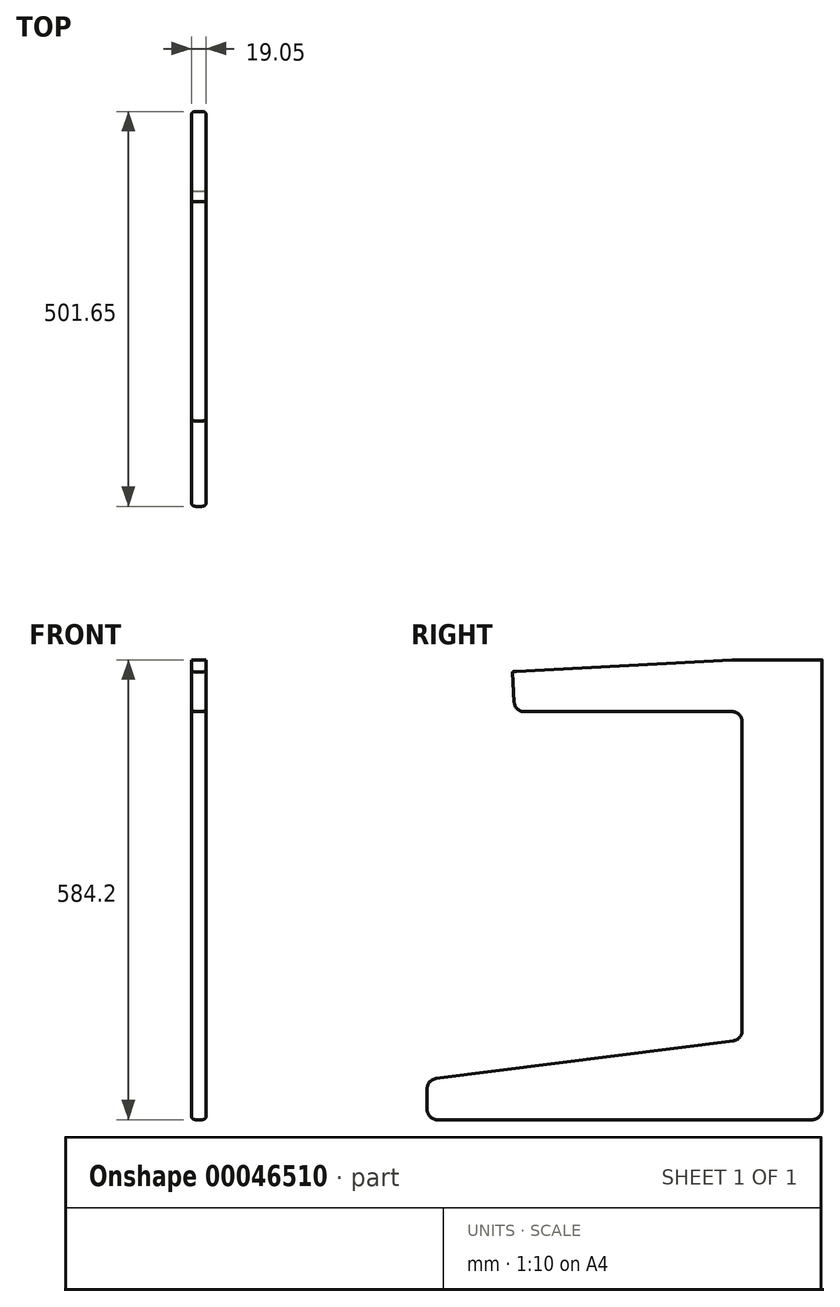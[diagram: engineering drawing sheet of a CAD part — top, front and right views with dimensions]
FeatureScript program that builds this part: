
annotation { "Feature Type Name" : "Feature", "Feature Type Description" : "" }
export const myFeature = defineFeature(function(context is Context, id is Id, definition is map)
    precondition{}
    {
        {
            var Q0;
            Q0=qCreatedBy(makeId("Right.planeOp"),FACE);
            var sketch = newSketch(context, id + "F0", { "sketchPlane" : qUnion([Q0])});
            skLineSegment(sketch, "E0", {"start": v(282.08, -321.8) * mm, "end": v(282.08, 249.7) * mm});
            skLineSegment(sketch, "E1", {"start": v(282.08, 249.7) * mm, "end": v(167.78, 249.7) * mm});
            skLineSegment(sketch, "E2", {"start": v(167.78, 249.7) * mm, "end": v(-111.2, 234.5) * mm});
            skLineSegment(sketch, "E3", {"start": v(-111.2, 234.5) * mm, "end": v(-109.1, 195.79) * mm});
            skLineSegment(sketch, "E4", {"start": v(-96.41, 183.78) * mm, "end": v(167.78, 183.78) * mm});
            skLineSegment(sketch, "E5", {"start": v(180.48, 171.08) * mm, "end": v(180.48, -221.72) * mm});
            skLineSegment(sketch, "E6", {"start": v(169.38, -234.32) * mm, "end": v(-208.47, -282.3) * mm});
            skLineSegment(sketch, "E7", {"start": v(-219.57, -294.9) * mm, "end": v(-219.57, -321.8) * mm});
            skLineSegment(sketch, "E8", {"start": v(-206.87, -334.5) * mm, "end": v(269.38, -334.5) * mm});
            skPoint(sketch, "E9.visualSharp", {"position": v(180.48, 183.78) * mm});
            skArc(sketch, "E9.filletArc", {"start": v(180.48, 171.08) * mm, "mid": v(176.76, 180.06) * mm, "end": v(167.78, 183.78) * mm});
            skPoint(sketch, "E10.visualSharp", {"position": v(-108.44, 183.78) * mm});
            skArc(sketch, "E10.filletArc", {"start": v(-109.1, 195.79) * mm, "mid": v(-105.15, 187.26) * mm, "end": v(-96.41, 183.78) * mm});
            skPoint(sketch, "E11.visualSharp", {"position": v(180.48, -232.9) * mm});
            skArc(sketch, "E11.filletArc", {"start": v(169.38, -234.32) * mm, "mid": v(177.31, -230.12) * mm, "end": v(180.48, -221.72) * mm});
            skPoint(sketch, "E12.visualSharp", {"position": v(-219.57, -283.7) * mm});
            skArc(sketch, "E12.filletArc", {"start": v(-208.47, -282.3) * mm, "mid": v(-216.4, -286.5) * mm, "end": v(-219.57, -294.9) * mm});
            skPoint(sketch, "E13.visualSharp", {"position": v(-219.57, -334.5) * mm});
            skArc(sketch, "E13.filletArc", {"start": v(-219.57, -321.8) * mm, "mid": v(-215.85, -330.79) * mm, "end": v(-206.87, -334.5) * mm});
            skPoint(sketch, "E14.visualSharp", {"position": v(282.08, -334.5) * mm});
            skArc(sketch, "E14.filletArc", {"start": v(269.38, -334.5) * mm, "mid": v(278.36, -330.79) * mm, "end": v(282.08, -321.8) * mm});
            skSolve(sketch);
        }
        {
            var Q0;
            Q0 = qSketchRegion(id + "F0", true);
            extrude(context, id + "F1", {"entities" : qUnion([Q0]), "depth" : 19.05 * mm});
        }
        {
            var Q0;
            Q0=makeQuery(id+"F1.opExtrude","CAP_EDGE",EDGE,{"disambiguationData":[OSD([sQuery(id+"F0.wireOp",EDGE,"E3")])],"isStart":false});
            var Q1;
            Q1=makeQuery(id+"F1.opExtrude","CAP_EDGE",EDGE,{"disambiguationData":[OSD([sQuery(id+"F0.wireOp",EDGE,"E3")])],"isStart":true});
            fillet(context, id + "F2", {"entities" : qUnion([Q0, Q1]), "radius" : 5.08 * mm, "tangentPropagation" : true, "allowEdgeOverflow" : false});
        }
    });
